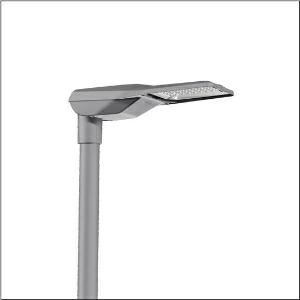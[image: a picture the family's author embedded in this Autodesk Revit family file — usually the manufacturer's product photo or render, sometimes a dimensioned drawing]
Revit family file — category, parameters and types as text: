
# Revit family: streetlight_sl_21_iq_mini___st0_8a_5xe2c41d08hb_7f29
name_source: partatom
category: Lighting Fixtures
units: mm (PartAtom-declared; Revit-internal decimal feet)

## family parameters
Cut with Voids When Loaded = No
Host = Face
Light Source = No
Part Type = Normal
Room Calculation Point = No
Round Connector Dimension = Use Diameter
Shared = No

## types (1)
- --- (1 x LED, 9860 lm, 70.9 W, 4000K)
    Apparent Load = 71 VA
    CIE Flux Codes = 38 75 97 100 100
    Color Rendering = 70
    Color Temperature = 4000K
    Default Elevation = 1800 mm
    Description = Streetlight SL 21 iQ mini, mast luminaire, primary light control with lens, of PMMA, primary optical cover: cover, of toughened safety glass, transparent, light distribution: ST0.8a, light emission: direct distribution, primary light characteristic: asymmetric, installation type: post-top, side-entry, LED, High Power LED, rated luminous flux: 9.860lm, luminous efficacy: 139lm/W, light colour: 740, colour temperature: 4000K, control: Auto-Match, Temp-Guard, Lumen-Switch, Night-Set, Smart-Wire, Light-Fading, Desk-Remote (wireless, voltage-free reading and setting of iQ features in the workshop via application-optimized NFC function/RFID function), optimised constant luminous flux control (CLO 2.0), presetting dimming linear, mains connection: 220..240V, AC, 50/60Hz, start of lifetime: 71W, end of service life: 75W, reduction: 31W, luminaire housing, of diecast aluminium, powder-coated, Siteco® metallic grey (DB 702S), corrosivity category C5 mid according to DIN EN ISO 12944, please order mast flange separately, inclination adjustable: 0°, 5°, 10°, 15°, sealing non-destructively replaceable, multi-level sealing system, length: 628mm, width: 235mm, height: 110mm, mast flange for spigot size: 42mm (side-entry): 5XC10008XM4, 60/48mm (side-entry/post-top): 5XC10108XM2, 76/60mm (side-entry/post-top): 5XC10108XM1, protection rating (complete): IP66, insulation class (complete): insulation class II (safety insulation), certification: CE, ENEC, ENEC+, VDE, impact resistance: IK09, permissible operating ambient temperature for outdoor applications: -40..+50°C, standard-compliant lighting for roads and squares, packaging unit: 1 piece

Light Distribution: ST0.8a
    Height = 110 mm
    Lamp = 1 x LED
    Lamp Light Flux = 9860 lm
    Lamp Power = 70.9 W
    Lamp count = 1
    Length = 625 mm
    Luminous efficacy = 139 lm/W
    Manufacturer = Siteco
    ModVariant = No
    Model = 5XE2C41D08HB
    Number of Poles = 1
    OnlyDefault = Yes
    Power Factor = 1
    Product Name = Streetlight SL 21 iQ mini | ST0.8a
    Product group = mast luminaire | pylon top
    ProductGroupID = 6100
    Protection Class = Protection class II
    Protection Degree = IP 66
    RLX_Detail_Level = 1
    RLX_Emergency_Light_Flux = 0 lm
    RLX_Emergency_Type = 0
    RLX_Emergency_Type_DB = No
    RlxData = <blob elided: 92273 chars, md5=62c16453>
    Socket = socket
    Standby Power = 0 W
    System Light Flux = 9860 lm
    System Power = 71 W
    Type Comments = factory setting: luminous flux: 100 % | dim-lin: 254 | 711 mA
    Type Image = l_1003519.jpg
    URL = http://relux.com
    VarID = @adj_089697
    Voltage = 0 V
    Weight = 0.00 kg
    Width = 234 mm

## geometry (parser evidence)
native form markers: Blend x4, Sweep x10
no freeform markers — native parametric forms only
